# Revit family: KR6080001_Portarollos Koral
name_source: partatom
category: Furniture
units: mm (PartAtom-declared; Revit-internal decimal feet)

## family parameters
Always vertical = Yes
Cut with Voids When Loaded = No
Host = Wall
OmniClass Number = 23.31.25.00
OmniClass Title = Toilet and Bath Specialties
Room Calculation Point = No
Shared = No

## types (1)
- Niquel
    Alto = 500 mm  [stored 1.64042 ft]
    Colección = Koral
    Creado por = BIMBAU
    Default Elevation = 0 mm  [stored 0 ft]
    Description = Un accesorio que posee una combinación de trazos rectos y curvos que le dan el toque perfecto a su baño, ¿qué esperas para tenerlo?
    Fecha de creación = 08/04/2021
    Garantía = 30 años en estructura
    Garantía Acabados = 3 años en acabado
    Manufacturer = Corona
    Material = Corona_Cromado
    Referencia = KR6080001
    Resistencia = Resistente a la corrosión, pelado y decoloración por agua
    Temperatura de uso = De 4º C a 40º C (40º F y 104º F)
    URL = https://corona.co

note: [stored X ft] marks values corroborated as IEEE doubles in the binary element streams (Revit-internal decimal feet)

## geometry (parser evidence)
native form markers: Sweep x3
no freeform markers — native parametric forms only
